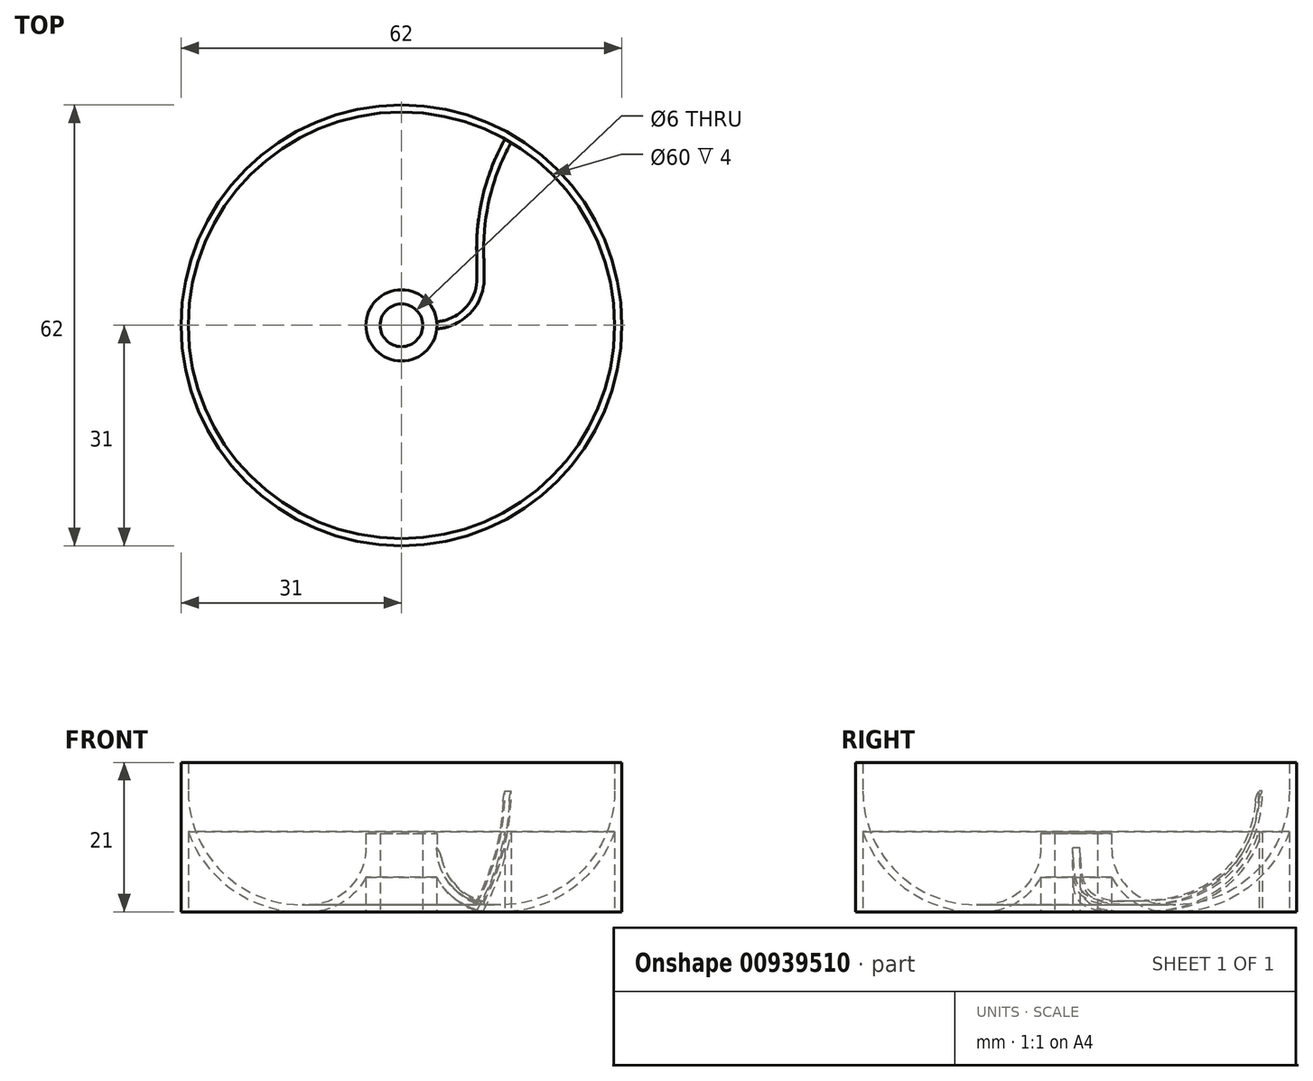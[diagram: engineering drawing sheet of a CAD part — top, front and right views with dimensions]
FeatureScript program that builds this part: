
annotation { "Feature Type Name" : "Feature", "Feature Type Description" : "" }
export const myFeature = defineFeature(function(context is Context, id is Id, definition is map)
    precondition{}
    {
        {
            var Q0;
            Q0=qCreatedBy(makeId("Front.planeOp"),FACE);
            var sketch = newSketch(context, id + "F0", { "sketchPlane" : qUnion([Q0])});
            skLineSegment(sketch, "E0.bottom", {"start": v(-31, 21) * mm, "end": v(-30, 21) * mm});
            skLineSegment(sketch, "E0.top", {"start": v(-31, 0) * mm, "end": v(-30, 0) * mm});
            skLineSegment(sketch, "E0.left", {"start": v(-31, 21) * mm, "end": v(-31, 0) * mm});
            skLineSegment(sketch, "E0.right", {"start": v(-3, 11) * mm, "end": v(-3, 0) * mm});
            skLineSegment(sketch, "E1", {"start": v(-14, 1) * mm, "end": v(-13, 1) * mm});
            skLineSegment(sketch, "E2", {"start": v(-5, 9) * mm, "end": v(-5, 11) * mm});
            skLineSegment(sketch, "E3.trimOffspring", {"start": v(-5, 11) * mm, "end": v(-3, 11) * mm});
            skArc(sketch, "E4.filletArc", {"start": v(-13, 1) * mm, "mid": v(-7.34, 3.34) * mm, "end": v(-5, 9) * mm});
            skArc(sketch, "E5", {"start": v(-30, 17) * mm, "mid": v(-25.31, 5.69) * mm, "end": v(-14, 1) * mm});
            skLineSegment(sketch, "E6", {"start": v(-30, 21) * mm, "end": v(-30, 17) * mm});
            skLineSegment(sketch, "E7", {"start": v(0, 0) * mm, "end": v(0, 21) * mm, "construction": true});
            skLineSegment(sketch, "E8.0", {"start": v(-30, 11.26) * mm, "end": v(-30, 0) * mm});
            skLineSegment(sketch, "E8.1", {"start": v(-5, 4.88) * mm, "end": v(-5, 0) * mm});
            skArc(sketch, "E8.2", {"start": v(-13, 0) * mm, "mid": v(-8.32, 1.32) * mm, "end": v(-5, 4.88) * mm});
            skLineSegment(sketch, "E8.3", {"start": v(-14, 0) * mm, "end": v(-13, 0) * mm});
            skArc(sketch, "E8.4", {"start": v(-30, 11.26) * mm, "mid": v(-23.78, 3.1) * mm, "end": v(-14, 0) * mm});
            skLineSegment(sketch, "E9.trimOffspring", {"start": v(-5, 0) * mm, "end": v(-3, 0) * mm});
            skLineSegment(sketch, "E10", {"start": v(-5, 0) * mm, "end": v(-5, 11) * mm, "construction": true});
            skSolve(sketch);
        }
        {
            var Q0;
            Q0=makeQuery(id+"F0.imprint","IMPRINT",FACE,{"disambiguationData":[TD([[makeQuery(id+"F0.imprint","IMPRINT",EDGE,{"derivedFrom":sQuery(id+"F0.wireOp",EDGE,"E0.bottom")}),-1.0]])]});
            var Q1;
            Q1=sQuery(id+"F0.wireOp",EDGE,"E7");
            revolve(context, id + "F1", {"surfaceOperationType" : NewSurfaceOperationType.NEW, "entities" : qUnion([Q0]), "axis" : qUnion([Q1]), "revolveType" : RevolveType.FULL});
        }
        {
            var Q0;
            Q0=qCreatedBy(makeId("Top.planeOp"),FACE);
            var sketch = newSketch(context, id + "F2", { "sketchPlane" : qUnion([Q0])});
            skLineSegment(sketch, "E11.bottom", {"start": v(2, -5) * mm, "end": v(7, -5) * mm, "construction": true});
            skLineSegment(sketch, "E11.top", {"start": v(2, 0) * mm, "end": v(7, 0) * mm, "construction": true});
            skLineSegment(sketch, "E11.left", {"start": v(2, -5) * mm, "end": v(2, 0) * mm, "construction": true});
            skLineSegment(sketch, "E11.right", {"start": v(7, -5) * mm, "end": v(7, 0) * mm, "construction": true});
            skLineSegment(sketch, "E12.bottom", {"start": v(7, -5) * mm, "end": v(-1, -5) * mm, "construction": true});
            skLineSegment(sketch, "E12.top", {"start": v(7, -13) * mm, "end": v(-1, -13) * mm, "construction": true});
            skLineSegment(sketch, "E12.left", {"start": v(7, -5) * mm, "end": v(7, -13) * mm, "construction": true});
            skLineSegment(sketch, "E12.right", {"start": v(-1, -5) * mm, "end": v(-1, -13) * mm, "construction": true});
            skLineSegment(sketch, "E13.bottom", {"start": v(-1, -13) * mm, "end": v(-14, -13) * mm, "construction": true});
            skLineSegment(sketch, "E13.top", {"start": v(-1, 0) * mm, "end": v(-14, 0) * mm, "construction": true});
            skLineSegment(sketch, "E13.left", {"start": v(-1, -13) * mm, "end": v(-1, 0) * mm, "construction": true});
            skLineSegment(sketch, "E13.right", {"start": v(-14, -13) * mm, "end": v(-14, 0) * mm, "construction": true});
            skLineSegment(sketch, "E14.bottom", {"start": v(-14, 0) * mm, "end": v(7, 0) * mm, "construction": true});
            skLineSegment(sketch, "E14.top", {"start": v(-14, 21) * mm, "end": v(7, 21) * mm, "construction": true});
            skLineSegment(sketch, "E14.left", {"start": v(-14, 0) * mm, "end": v(-14, 21) * mm, "construction": true});
            skLineSegment(sketch, "E14.right", {"start": v(7, 0) * mm, "end": v(7, 21) * mm, "construction": true});
            skLineSegment(sketch, "E15.bottom", {"start": v(7, -13) * mm, "end": v(41, -13) * mm, "construction": true});
            skLineSegment(sketch, "E15.top", {"start": v(7, 21) * mm, "end": v(41, 21) * mm, "construction": true});
            skLineSegment(sketch, "E15.left", {"start": v(7, -13) * mm, "end": v(7, 21) * mm, "construction": true});
            skLineSegment(sketch, "E15.right", {"start": v(41, -13) * mm, "end": v(41, 21) * mm, "construction": true});
            skLineSegment(sketch, "E16", {"start": v(0, 0) * mm, "end": v(2, 0) * mm, "construction": true});
            skArc(sketch, "E17", {"start": v(7, -5) * mm, "mid": v(6.32, -2.48) * mm, "end": v(4.45, -0.64) * mm, "construction": true});
            skArc(sketch, "E18", {"start": v(-1, -13) * mm, "mid": v(4.66, -10.66) * mm, "end": v(7, -5) * mm, "construction": true});
            skArc(sketch, "E19", {"start": v(-14, 0) * mm, "mid": v(-10.2, -9.2) * mm, "end": v(-1, -13) * mm, "construction": true});
            skArc(sketch, "E20", {"start": v(7, 21) * mm, "mid": v(-7.85, 14.85) * mm, "end": v(-14, 0) * mm, "construction": true});
            skArc(sketch, "E21", {"start": v(26.73, 14.7) * mm, "mid": v(17.36, 19.38) * mm, "end": v(7, 21) * mm, "construction": true});
            skCircle(sketch, "E22", {"center": v(0, 0) * mm, "radius": 4.5 * mm, "construction": true});
            skCircle(sketch, "E23", {"center": v(0, 0) * mm, "radius": 30.5 * mm, "construction": true});
            skArc(sketch, "E24.0", {"start": v(8, -5) * mm, "mid": v(7.04, -1.75) * mm, "end": v(4.48, 0.47) * mm});
            skArc(sketch, "E24.1", {"start": v(25.52, 16.7) * mm, "mid": v(16.63, 20.65) * mm, "end": v(7, 22) * mm});
            skArc(sketch, "E24.2", {"start": v(7, 22) * mm, "mid": v(-8.56, 15.56) * mm, "end": v(-15, 0) * mm});
            skArc(sketch, "E24.3", {"start": v(-15, 0) * mm, "mid": v(-10.9, -9.9) * mm, "end": v(-1, -14) * mm});
            skArc(sketch, "E24.4", {"start": v(-1, -14) * mm, "mid": v(5.36, -11.36) * mm, "end": v(8, -5) * mm});
            skArc(sketch, "E25.0", {"start": v(6, -5) * mm, "mid": v(5.52, -3.1) * mm, "end": v(4.19, -1.65) * mm});
            skArc(sketch, "E25.1", {"start": v(27.75, 12.66) * mm, "mid": v(18, 18.11) * mm, "end": v(7, 20) * mm});
            skArc(sketch, "E25.2", {"start": v(7, 20) * mm, "mid": v(-7.14, 14.14) * mm, "end": v(-13, 0) * mm});
            skArc(sketch, "E25.3", {"start": v(-13, 0) * mm, "mid": v(-9.49, -8.49) * mm, "end": v(-1, -12) * mm});
            skArc(sketch, "E25.4", {"start": v(-1, -12) * mm, "mid": v(3.95, -9.95) * mm, "end": v(6, -5) * mm});
            skArc(sketch, "E26", {"start": v(4.19, -1.65) * mm, "mid": v(4.46, -0.6) * mm, "end": v(4.48, 0.47) * mm});
            skArc(sketch, "E27", {"start": v(27.75, 12.66) * mm, "mid": v(26.71, 14.72) * mm, "end": v(25.52, 16.7) * mm});
            skSolve(sketch);
        }
        {
            var Q0;
            Q0=qCreatedBy(makeId("Top.planeOp"),FACE);
            var sketch = newSketch(context, id + "F3", { "sketchPlane" : qUnion([Q0])});
            skCircle(sketch, "E28", {"center": v(0, 0) * mm, "radius": 4.5 * mm, "construction": true});
            skCircle(sketch, "E29", {"center": v(0, 0) * mm, "radius": 30.5 * mm, "construction": true});
            skLineSegment(sketch, "E30", {"start": v(0, 0) * mm, "end": v(30.5, 0) * mm, "construction": true});
            skLineSegment(sketch, "E31", {"start": v(15.25, 26.41) * mm, "end": v(2.25, 3.9) * mm, "construction": true});
            skLineSegment(sketch, "E32", {"start": v(11.07, 10.34) * mm, "end": v(11.13, 6.72) * mm, "construction": true});
            skArc(sketch, "E33", {"start": v(4.5, 0) * mm, "mid": v(9.22, 1.98) * mm, "end": v(11.13, 6.72) * mm, "construction": true});
            skArc(sketch, "E34", {"start": v(15.25, 26.41) * mm, "mid": v(12.07, 18.66) * mm, "end": v(11.07, 10.34) * mm, "construction": true});
            skPoint(sketch, "E35", {"position": v(11.1, 8.53) * mm});
            skArc(sketch, "E36.0", {"start": v(4.47, 0.5) * mm, "mid": v(8.85, 2.32) * mm, "end": v(10.63, 6.72) * mm});
            skLineSegment(sketch, "E36.1", {"start": v(10.57, 10.33) * mm, "end": v(10.63, 6.72) * mm});
            skArc(sketch, "E36.2", {"start": v(14.81, 26.66) * mm, "mid": v(11.59, 18.78) * mm, "end": v(10.57, 10.33) * mm});
            skArc(sketch, "E37.0", {"start": v(4.47, -0.5) * mm, "mid": v(9.57, 1.61) * mm, "end": v(11.63, 6.73) * mm});
            skLineSegment(sketch, "E37.1", {"start": v(11.57, 10.35) * mm, "end": v(11.63, 6.73) * mm});
            skArc(sketch, "E37.2", {"start": v(15.68, 26.16) * mm, "mid": v(12.56, 18.53) * mm, "end": v(11.57, 10.35) * mm});
            skArc(sketch, "E38", {"start": v(4.47, -0.5) * mm, "mid": v(4.5, 0) * mm, "end": v(4.47, 0.5) * mm});
            skArc(sketch, "E39", {"start": v(15.68, 26.16) * mm, "mid": v(15.25, 26.41) * mm, "end": v(14.81, 26.66) * mm});
            skSolve(sketch);
        }
        {
            var Q0;
            Q0 = qSketchRegion(id + "F3", true);
            extrude(context, id + "F4", {"entities" : qUnion([Q0]), "operationType" : NewBodyOperationType.ADD, "depth" : 17 * mm, "offsetDistance" : 25 * mm});
        }
        {
            var Q0;
            Q0=qCreatedBy(makeId("Front.planeOp"),FACE);
            var sketch = newSketch(context, id + "F5", { "sketchPlane" : qUnion([Q0])});
            skArc(sketch, "E40.0", {"start": v(-13, 1.5) * mm, "mid": v(-8.2, 3.24) * mm, "end": v(-5.62, 7.65) * mm});
            skLineSegment(sketch, "E40.1", {"start": v(-14, 1.5) * mm, "end": v(-13, 1.5) * mm});
            skArc(sketch, "E40.2", {"start": v(-29.43, 15.5) * mm, "mid": v(-24.42, 5.52) * mm, "end": v(-14, 1.5) * mm});
            skLineSegment(sketch, "E41", {"start": v(-30, 17) * mm, "end": v(-30, 21) * mm});
            skLineSegment(sketch, "E42", {"start": v(-5, 9) * mm, "end": v(-5, 11) * mm});
            skLineSegment(sketch, "E43", {"start": v(-5, 11) * mm, "end": v(-3, 11) * mm});
            skLineSegment(sketch, "E44", {"start": v(-3, 11) * mm, "end": v(-3, 21) * mm});
            skLineSegment(sketch, "E45", {"start": v(-3, 21) * mm, "end": v(-30, 21) * mm});
            skArc(sketch, "E46.filletArc", {"start": v(-29.43, 15.5) * mm, "mid": v(-29.61, 16.3) * mm, "end": v(-30, 17) * mm});
            skArc(sketch, "E47.filletArc", {"start": v(-5, 9) * mm, "mid": v(-5.4, 8.36) * mm, "end": v(-5.62, 7.65) * mm});
            skSolve(sketch);
        }
        {
            var Q0;
            Q0 = qSketchRegion(id + "F5", true);
            var Q1;
            Q1=sQuery(id+"F0.wireOp",EDGE,"E7");
            revolve(context, id + "F6", {"operationType" : NewBodyOperationType.REMOVE, "surfaceOperationType" : NewSurfaceOperationType.NEW, "entities" : qUnion([Q0]), "axis" : qUnion([Q1]), "revolveType" : RevolveType.FULL});
        }
    });
